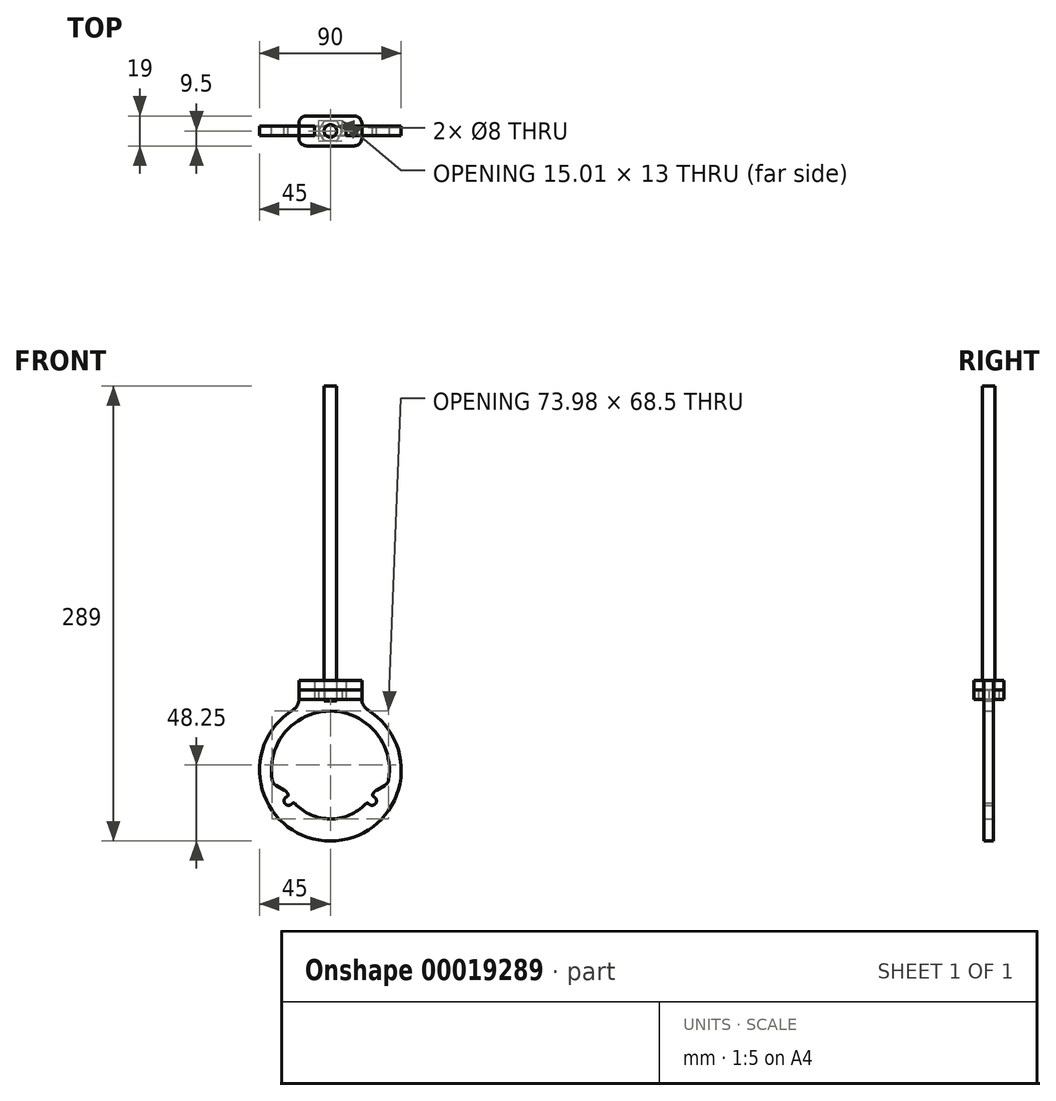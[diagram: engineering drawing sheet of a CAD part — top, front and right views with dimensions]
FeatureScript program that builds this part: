
annotation { "Feature Type Name" : "Feature", "Feature Type Description" : "" }
export const myFeature = defineFeature(function(context is Context, id is Id, definition is map)
    precondition{}
    {
        {
            var Q0;
            Q0=qCreatedBy(makeId("Front.planeOp"),FACE);
            var sketch = newSketch(context, id + "F0", { "sketchPlane" : qUnion([Q0])});
            skCircle(sketch, "E0", {"center": v(0, 0) * mm, "radius": 30 * mm, "construction": true});
            skArc(sketch, "E1", {"start": v(-29.8, -8.57) * mm, "mid": v(-33.82, -12.34) * mm, "end": v(-28.3, -12.64) * mm});
            skArc(sketch, "E2", {"start": v(-28.3, -12.64) * mm, "mid": v(0, -31) * mm, "end": v(28.3, -12.64) * mm});
            skArc(sketch, "E3.trimOffspring", {"start": v(29.8, -8.57) * mm, "mid": v(30.21, -6.95) * mm, "end": v(30.54, -5.31) * mm});
            skArc(sketch, "E4.trimOffspring", {"start": v(28.3, -12.64) * mm, "mid": v(33.82, -12.34) * mm, "end": v(29.8, -8.57) * mm});
            skArc(sketch, "E5.trimOffspring", {"start": v(34.92, 2.37) * mm, "mid": v(0, 35) * mm, "end": v(-34.92, 2.37) * mm});
            skArc(sketch, "E6", {"start": v(-34.92, 2.37) * mm, "mid": v(-33.89, -2.13) * mm, "end": v(-30.54, -5.31) * mm});
            skLineSegment(sketch, "E7", {"start": v(0, -11.31) * mm, "end": v(0, 0) * mm, "construction": true});
            skArc(sketch, "E8.0.MirrorCS", {"start": v(34.92, 2.37) * mm, "mid": v(33.89, -2.13) * mm, "end": v(30.54, -5.31) * mm});
            skArc(sketch, "E9.trimOffspring", {"start": v(-30.54, -5.31) * mm, "mid": v(-30.21, -6.95) * mm, "end": v(-29.8, -8.57) * mm});
            skLineSegment(sketch, "E10", {"start": v(-30.54, -5.31) * mm, "end": v(30.54, -5.31) * mm, "construction": true});
            skLineSegment(sketch, "E11", {"start": v(-31, -11.31) * mm, "end": v(31, -11.31) * mm, "construction": true});
            skLineSegment(sketch, "E12", {"start": v(-20, 57) * mm, "end": v(-10, 57) * mm});
            skLineSegment(sketch, "E13", {"start": v(20, 57) * mm, "end": v(20, 40.31) * mm});
            skLineSegment(sketch, "E14", {"start": v(-20, 57) * mm, "end": v(-20, 40.31) * mm});
            skPoint(sketch, "E15", {"position": v(0, 57) * mm});
            skArc(sketch, "E16", {"start": v(-20, 40.31) * mm, "mid": v(0, -45) * mm, "end": v(20, 40.31) * mm});
            skArc(sketch, "E17", {"start": v(20, 40.31) * mm, "mid": v(0, 45) * mm, "end": v(-20, 40.31) * mm, "construction": true});
            skLineSegment(sketch, "E18", {"start": v(-10, 57) * mm, "end": v(-10, 45) * mm});
            skLineSegment(sketch, "E19", {"start": v(10, 45) * mm, "end": v(10, 57) * mm});
            skLineSegment(sketch, "E20", {"start": v(-10, 45) * mm, "end": v(-4, 45) * mm});
            skLineSegment(sketch, "E21", {"start": v(10, 57) * mm, "end": v(20, 57) * mm});
            skLineSegment(sketch, "E22", {"start": v(-10, 57) * mm, "end": v(10, 57) * mm, "construction": true});
            skLineSegment(sketch, "E23", {"start": v(4, 45) * mm, "end": v(4, 44) * mm});
            skLineSegment(sketch, "E24", {"start": v(4, 44) * mm, "end": v(-4, 44) * mm});
            skLineSegment(sketch, "E25", {"start": v(-4, 44) * mm, "end": v(-4, 45) * mm});
            skLineSegment(sketch, "E26", {"start": v(4, 45) * mm, "end": v(10, 45) * mm});
            skLineSegment(sketch, "E27", {"start": v(-4, 45) * mm, "end": v(4, 45) * mm, "construction": true});
            skSolve(sketch);
        }
        {
            var Q0;
            Q0=qCreatedBy(makeId("Front.planeOp"),FACE);
            var sketch = newSketch(context, id + "F1", { "sketchPlane" : qUnion([Q0])});
            skArc(sketch, "E28.0", {"start": v(-20, 40.31) * mm, "mid": v(0, -45) * mm, "end": v(20, 40.31) * mm});
            skLineSegment(sketch, "E28.1", {"start": v(20, 57) * mm, "end": v(20, 40.31) * mm});
            skLineSegment(sketch, "E28.2", {"start": v(10, 57) * mm, "end": v(20, 57) * mm});
            skLineSegment(sketch, "E28.3", {"start": v(10, 45) * mm, "end": v(10, 57) * mm});
            skLineSegment(sketch, "E28.4", {"start": v(4, 45) * mm, "end": v(10, 45) * mm});
            skLineSegment(sketch, "E28.5", {"start": v(4, 45) * mm, "end": v(4, 44) * mm});
            skLineSegment(sketch, "E28.6", {"start": v(4, 44) * mm, "end": v(-4, 44) * mm});
            skLineSegment(sketch, "E28.7", {"start": v(-4, 44) * mm, "end": v(-4, 45) * mm});
            skLineSegment(sketch, "E28.8", {"start": v(-10, 45) * mm, "end": v(-4, 45) * mm});
            skLineSegment(sketch, "E28.9", {"start": v(-10, 57) * mm, "end": v(-10, 45) * mm});
            skLineSegment(sketch, "E28.10", {"start": v(-20, 57) * mm, "end": v(-10, 57) * mm});
            skLineSegment(sketch, "E28.11", {"start": v(-20, 57) * mm, "end": v(-20, 40.31) * mm});
            skCircle(sketch, "E29.0", {"center": v(0, 0) * mm, "radius": 30 * mm, "construction": true});
            skLineSegment(sketch, "E30", {"start": v(-37.5, 0) * mm, "end": v(37.5, 0) * mm, "construction": true});
            skLineSegment(sketch, "E31", {"start": v(-34.98, -13.52) * mm, "end": v(34.98, -13.52) * mm, "construction": true});
            skLineSegment(sketch, "E32", {"start": v(-32.02, -19.52) * mm, "end": v(32.02, -19.52) * mm, "construction": true});
            skLineSegment(sketch, "E33", {"start": v(0, 37.5) * mm, "end": v(0, -37.5) * mm, "construction": true});
            skLineSegment(sketch, "E34", {"start": v(-27.9, -13.52) * mm, "end": v(-36.51, -8.54) * mm});
            skLineSegment(sketch, "E35.0.MirrorCS", {"start": v(27.9, -13.52) * mm, "end": v(36.51, -8.54) * mm});
            skArc(sketch, "E36", {"start": v(27.9, -13.52) * mm, "mid": v(0, 31) * mm, "end": v(-27.9, -13.52) * mm, "construction": true});
            skArc(sketch, "E37", {"start": v(-27.9, -13.52) * mm, "mid": v(-27.05, -15.14) * mm, "end": v(-26.11, -16.7) * mm});
            skArc(sketch, "E38", {"start": v(-36.51, -8.54) * mm, "mid": v(0, -37.5) * mm, "end": v(36.51, -8.54) * mm, "construction": true});
            skArc(sketch, "E39", {"start": v(36.51, -8.54) * mm, "mid": v(0, 37.5) * mm, "end": v(-36.51, -8.54) * mm});
            skArc(sketch, "E40", {"start": v(26.13, -16.68) * mm, "mid": v(27.06, -15.13) * mm, "end": v(27.9, -13.52) * mm});
            skArc(sketch, "E41", {"start": v(23.63, -20.07) * mm, "mid": v(24.94, -18.42) * mm, "end": v(26.13, -16.68) * mm, "construction": true});
            skArc(sketch, "E42", {"start": v(-23.75, -19.92) * mm, "mid": v(-0.1, -31) * mm, "end": v(23.63, -20.07) * mm});
            skArc(sketch, "E43", {"start": v(-26.11, -16.7) * mm, "mid": v(-24.99, -18.35) * mm, "end": v(-23.75, -19.92) * mm, "construction": true});
            skArc(sketch, "E44", {"start": v(-23.75, -19.92) * mm, "mid": v(-24.28, -17.83) * mm, "end": v(-26.11, -16.7) * mm, "construction": true});
            skArc(sketch, "E45", {"start": v(-26.11, -16.7) * mm, "mid": v(-28.87, -21.2) * mm, "end": v(-23.75, -19.92) * mm});
            skArc(sketch, "E46", {"start": v(23.63, -20.07) * mm, "mid": v(24.13, -17.82) * mm, "end": v(26.13, -16.68) * mm, "construction": true});
            skArc(sketch, "E47", {"start": v(26.13, -16.68) * mm, "mid": v(28.72, -21.21) * mm, "end": v(23.63, -20.07) * mm});
            skSolve(sketch);
        }
        {
            var Q0;
            Q0=qSketchRegion(id+"F1",true);
            extrude(context, id + "F2", {"entities" : qUnion([Q0]), "depth" : 6 * mm});
        }
        {
            var Q0;
            Q0=makeQuery(id+"F2.opExtrude","SWEPT_FACE",FACE,{"disambiguationData":[OSD([sQuery(id+"F1.wireOp",EDGE,"E28.4")])]});
            var sketch = newSketch(context, id + "F3", { "sketchPlane" : qUnion([Q0])});
            skLineSegment(sketch, "E48.bottom", {"start": v(20, -12.5) * mm, "end": v(-20, -12.5) * mm});
            skLineSegment(sketch, "E48.top", {"start": v(20, 6.5) * mm, "end": v(-20, 6.5) * mm});
            skLineSegment(sketch, "E48.left", {"start": v(20, -12.5) * mm, "end": v(20, -6) * mm});
            skLineSegment(sketch, "E48.right", {"start": v(-20, -12.5) * mm, "end": v(-20, -6) * mm});
            skCircle(sketch, "E49.cCircle", {"center": v(0, -3) * mm, "radius": 6.5 * mm, "construction": true});
            skLineSegment(sketch, "E49.0", {"start": v(-3.75, -9.5) * mm, "end": v(-7.5, -3) * mm});
            skLineSegment(sketch, "E49.1", {"start": v(-7.5, -3) * mm, "end": v(-3.75, 3.5) * mm});
            skLineSegment(sketch, "E49.2", {"start": v(-3.75, 3.5) * mm, "end": v(3.75, 3.5) * mm});
            skLineSegment(sketch, "E49.3", {"start": v(3.75, 3.5) * mm, "end": v(7.5, -3) * mm});
            skLineSegment(sketch, "E49.4", {"start": v(7.5, -3) * mm, "end": v(3.75, -9.5) * mm});
            skLineSegment(sketch, "E49.5", {"start": v(3.75, -9.5) * mm, "end": v(-3.75, -9.5) * mm});
            skPoint(sketch, "E49.0.midPoint", {"position": v(-5.63, -6.25) * mm});
            skLineSegment(sketch, "E50", {"start": v(10, -3) * mm, "end": v(-10, -3) * mm, "construction": true});
            skLineSegment(sketch, "E51", {"start": v(-10, 0) * mm, "end": v(-10, -6) * mm});
            skLineSegment(sketch, "E52.trimOffspring", {"start": v(20, 0) * mm, "end": v(20, 6.5) * mm});
            skLineSegment(sketch, "E53", {"start": v(-20, 0) * mm, "end": v(-10, 0) * mm});
            skLineSegment(sketch, "E54", {"start": v(-10, -6) * mm, "end": v(-20, -6) * mm});
            skLineSegment(sketch, "E55.trimOffspring", {"start": v(-20, 0) * mm, "end": v(-20, 6.5) * mm});
            skLineSegment(sketch, "E56", {"start": v(20, -6) * mm, "end": v(10, -6) * mm});
            skLineSegment(sketch, "E57", {"start": v(10, -6) * mm, "end": v(10, 0) * mm});
            skLineSegment(sketch, "E58", {"start": v(10, 0) * mm, "end": v(20, 0) * mm});
            skSolve(sketch);
        }
        {
            var Q0;
            Q0=qSketchRegion(id+"F3",true);
            extrude(context, id + "F4", {"entities" : qUnion([Q0]), "depth" : 6 * mm});
        }
        {
            var Q0;
            Q0=makeQuery(id+"F4.opExtrude","CAP_FACE",FACE,{"disambiguationData":[OSD([sQuery(id+"F3.wireOp",EDGE,"E48.bottom"),sQuery(id+"F3.wireOp",EDGE,"E48.top"),sQuery(id+"F3.wireOp",EDGE,"E48.left"),sQuery(id+"F3.wireOp",EDGE,"E48.right"),sQuery(id+"F3.wireOp",EDGE,"E49.0"),sQuery(id+"F3.wireOp",EDGE,"E49.1"),sQuery(id+"F3.wireOp",EDGE,"E49.2"),sQuery(id+"F3.wireOp",EDGE,"E49.3"),sQuery(id+"F3.wireOp",EDGE,"E49.4"),sQuery(id+"F3.wireOp",EDGE,"E49.5"),sQuery(id+"F3.wireOp",EDGE,"E52.trimOffspring"),sQuery(id+"F3.wireOp",EDGE,"E53"),sQuery(id+"F3.wireOp",EDGE,"E51"),sQuery(id+"F3.wireOp",EDGE,"E54"),sQuery(id+"F3.wireOp",EDGE,"E55.trimOffspring"),sQuery(id+"F3.wireOp",EDGE,"E56"),sQuery(id+"F3.wireOp",EDGE,"E57"),sQuery(id+"F3.wireOp",EDGE,"E58")])],"isStart":false});
            var sketch = newSketch(context, id + "F5", { "sketchPlane" : qUnion([Q0])});
            skLineSegment(sketch, "E59", {"start": v(20, -12.5) * mm, "end": v(20, -6) * mm});
            skLineSegment(sketch, "E60", {"start": v(20, -6) * mm, "end": v(10, -6) * mm});
            skLineSegment(sketch, "E61", {"start": v(10, -6) * mm, "end": v(10, 0) * mm});
            skLineSegment(sketch, "E62", {"start": v(10, 0) * mm, "end": v(20, 0) * mm});
            skLineSegment(sketch, "E63", {"start": v(20, 0) * mm, "end": v(20, 6.5) * mm});
            skLineSegment(sketch, "E64", {"start": v(20, 6.5) * mm, "end": v(-20, 6.5) * mm});
            skLineSegment(sketch, "E65", {"start": v(-20, 6.5) * mm, "end": v(-20, 0) * mm});
            skLineSegment(sketch, "E66", {"start": v(-20, 0) * mm, "end": v(-10, 0) * mm});
            skLineSegment(sketch, "E67", {"start": v(-10, 0) * mm, "end": v(-10, -6) * mm});
            skLineSegment(sketch, "E68", {"start": v(-10, -6) * mm, "end": v(-20, -6) * mm});
            skLineSegment(sketch, "E69", {"start": v(-20, -6) * mm, "end": v(-20, -12.5) * mm});
            skLineSegment(sketch, "E70", {"start": v(-20, -12.5) * mm, "end": v(20, -12.5) * mm});
            skCircle(sketch, "E71", {"center": v(0, -3) * mm, "radius": 4 * mm});
            skSolve(sketch);
        }
        {
            var Q0;
            Q0=qSketchRegion(id+"F5",true);
            extrude(context, id + "F6", {"entities" : qUnion([Q0]), "depth" : 6 * mm});
        }
        {
            var Q0;
            Q0=makeQuery(id+"F2.opExtrude","SWEPT_FACE",FACE,{"disambiguationData":[OSD([sQuery(id+"F1.wireOp",EDGE,"E28.6")])]});
            var sketch = newSketch(context, id + "F7", { "sketchPlane" : qUnion([Q0])});
            skCircle(sketch, "E72.0", {"center": v(0, -3) * mm, "radius": 4 * mm});
            skSolve(sketch);
        }
        {
            var Q0;
            Q0=qSketchRegion(id+"F7",true);
            extrude(context, id + "F8", {"entities" : qUnion([Q0]), "depth" : 200 * mm});
        }
        {
            var Q0;
            Q0=makeQuery(id+"F8.opExtrude","CAP_EDGE",EDGE,{"disambiguationData":[OSD([sQuery(id+"F7.wireOp",EDGE,"E72.0")])],"isStart":true});
            fillet(context, id + "F9", {"entities" : qUnion([Q0]), "radius" : 1 * mm, "tangentPropagation" : true, "allowEdgeOverflow" : false});
        }
        {
            var Q0;
            Q0=makeQuery(id+"F4.opExtrude","CAP_FACE",FACE,{"disambiguationData":[OSD([sQuery(id+"F3.wireOp",EDGE,"E48.bottom"),sQuery(id+"F3.wireOp",EDGE,"E48.top"),sQuery(id+"F3.wireOp",EDGE,"E48.left"),sQuery(id+"F3.wireOp",EDGE,"E48.right"),sQuery(id+"F3.wireOp",EDGE,"E49.0"),sQuery(id+"F3.wireOp",EDGE,"E49.1"),sQuery(id+"F3.wireOp",EDGE,"E49.2"),sQuery(id+"F3.wireOp",EDGE,"E49.3"),sQuery(id+"F3.wireOp",EDGE,"E49.4"),sQuery(id+"F3.wireOp",EDGE,"E49.5"),sQuery(id+"F3.wireOp",EDGE,"E52.trimOffspring"),sQuery(id+"F3.wireOp",EDGE,"E53"),sQuery(id+"F3.wireOp",EDGE,"E51"),sQuery(id+"F3.wireOp",EDGE,"E54"),sQuery(id+"F3.wireOp",EDGE,"E55.trimOffspring"),sQuery(id+"F3.wireOp",EDGE,"E56"),sQuery(id+"F3.wireOp",EDGE,"E57"),sQuery(id+"F3.wireOp",EDGE,"E58")])],"isStart":true});
            var sketch = newSketch(context, id + "F10", { "sketchPlane" : qUnion([Q0])});
            skLineSegment(sketch, "E73.0", {"start": v(-3.75, -3.5) * mm, "end": v(3.75, -3.5) * mm});
            skLineSegment(sketch, "E73.1", {"start": v(3.75, -3.5) * mm, "end": v(7.5, 3) * mm});
            skLineSegment(sketch, "E73.2", {"start": v(7.5, 3) * mm, "end": v(3.75, 9.5) * mm});
            skLineSegment(sketch, "E73.3", {"start": v(3.75, 9.5) * mm, "end": v(-3.75, 9.5) * mm});
            skLineSegment(sketch, "E73.4", {"start": v(-3.75, 9.5) * mm, "end": v(-7.5, 3) * mm});
            skLineSegment(sketch, "E73.5", {"start": v(-7.5, 3) * mm, "end": v(-3.75, -3.5) * mm});
            skCircle(sketch, "E74", {"center": v(0, 3) * mm, "radius": 4 * mm});
            skSolve(sketch);
        }
        {
            var Q0;
            Q0=qSketchRegion(id+"F10",true);
            extrude(context, id + "F11", {"entities" : qUnion([Q0]), "oppositeDirection" : true, "depth" : 6 * mm});
        }
        {
            var Q0;
            Q0=makeQuery(id+"F11.opExtrude","CAP_FACE",FACE,{"disambiguationData":[OSD([sQuery(id+"F10.wireOp",EDGE,"E73.0"),sQuery(id+"F10.wireOp",EDGE,"E73.1"),sQuery(id+"F10.wireOp",EDGE,"E73.2"),sQuery(id+"F10.wireOp",EDGE,"E73.3"),sQuery(id+"F10.wireOp",EDGE,"E73.4"),sQuery(id+"F10.wireOp",EDGE,"E73.5"),sQuery(id+"F10.wireOp",EDGE,"E74")])],"isStart":true});
            fillet(context, id + "F12", {"entities" : qUnion([Q0]), "radius" : .5 * mm, "tangentPropagation" : true, "allowEdgeOverflow" : false});
        }
        {
            var Q0;
            Q0=makeQuery(id+"F2.opExtrude","SWEPT_EDGE",EDGE,{"disambiguationData":[OSD([sQuery(id+"F1.wireOp",EDGE,"E34"),sQuery(id+"F1.wireOp",EDGE,"E39")])]});
            var Q1;
            Q1=makeQuery(id+"F2.opExtrude","SWEPT_EDGE",EDGE,{"disambiguationData":[OSD([sQuery(id+"F1.wireOp",EDGE,"E34"),sQuery(id+"F1.wireOp",EDGE,"E37")])]});
            var Q2;
            Q2=makeQuery(id+"F2.opExtrude","SWEPT_EDGE",EDGE,{"disambiguationData":[OSD([sQuery(id+"F1.wireOp",EDGE,"E35.0.MirrorCS"),sQuery(id+"F1.wireOp",EDGE,"E40")])]});
            var Q3;
            Q3=makeQuery(id+"F2.opExtrude","SWEPT_EDGE",EDGE,{"disambiguationData":[OSD([sQuery(id+"F1.wireOp",EDGE,"E35.0.MirrorCS"),sQuery(id+"F1.wireOp",EDGE,"E39")])]});
            var Q4;
            Q4=makeQuery(id+"F6.opExtrude","SWEPT_EDGE",EDGE,{"disambiguationData":[OSD([sQuery(id+"F5.wireOp",EDGE,"E59"),sQuery(id+"F5.wireOp",EDGE,"E70")])]});
            var Q5;
            Q5=makeQuery(id+"F4.opExtrude","SWEPT_EDGE",EDGE,{"disambiguationData":[OSD([sQuery(id+"F3.wireOp",EDGE,"E48.bottom"),sQuery(id+"F3.wireOp",EDGE,"E48.left")])]});
            var Q6;
            Q6=makeQuery(id+"F4.opExtrude","SWEPT_EDGE",EDGE,{"disambiguationData":[OSD([sQuery(id+"F3.wireOp",EDGE,"E48.top"),sQuery(id+"F3.wireOp",EDGE,"E52.trimOffspring")])]});
            var Q7;
            Q7=makeQuery(id+"F6.opExtrude","SWEPT_EDGE",EDGE,{"disambiguationData":[OSD([sQuery(id+"F5.wireOp",EDGE,"E63"),sQuery(id+"F5.wireOp",EDGE,"E64")])]});
            var Q8;
            Q8=makeQuery(id+"F4.opExtrude","SWEPT_EDGE",EDGE,{"disambiguationData":[OSD([sQuery(id+"F3.wireOp",EDGE,"E48.bottom"),sQuery(id+"F3.wireOp",EDGE,"E48.right")])]});
            var Q9;
            Q9=makeQuery(id+"F6.opExtrude","SWEPT_EDGE",EDGE,{"disambiguationData":[OSD([sQuery(id+"F5.wireOp",EDGE,"E69"),sQuery(id+"F5.wireOp",EDGE,"E70")])]});
            var Q10;
            Q10=makeQuery(id+"F6.opExtrude","SWEPT_EDGE",EDGE,{"disambiguationData":[OSD([sQuery(id+"F5.wireOp",EDGE,"E64"),sQuery(id+"F5.wireOp",EDGE,"E65")])]});
            var Q11;
            Q11=makeQuery(id+"F4.opExtrude","SWEPT_EDGE",EDGE,{"disambiguationData":[OSD([sQuery(id+"F3.wireOp",EDGE,"E48.top"),sQuery(id+"F3.wireOp",EDGE,"E55.trimOffspring")])]});
            fillet(context, id + "F13", {"entities" : qUnion([Q0, Q1, Q2, Q3, Q4, Q5, Q6, Q7, Q8, Q9, Q10, Q11]), "radius" : 5 * mm, "tangentPropagation" : true, "allowEdgeOverflow" : false});
        }
        {
            var Q0;
            Q0=makeQuery(id+"F2.opExtrude","SWEPT_EDGE",EDGE,{"disambiguationData":[OSD([sQuery(id+"F1.wireOp",EDGE,"E37"),sQuery(id+"F1.wireOp",EDGE,"E45")])]});
            var Q1;
            Q1=makeQuery(id+"F2.opExtrude","SWEPT_EDGE",EDGE,{"disambiguationData":[OSD([sQuery(id+"F1.wireOp",EDGE,"E42"),sQuery(id+"F1.wireOp",EDGE,"E45")])]});
            var Q2;
            Q2=makeQuery(id+"F2.opExtrude","SWEPT_EDGE",EDGE,{"disambiguationData":[OSD([sQuery(id+"F1.wireOp",EDGE,"E42"),sQuery(id+"F1.wireOp",EDGE,"E47")])]});
            var Q3;
            Q3=makeQuery(id+"F2.opExtrude","SWEPT_EDGE",EDGE,{"disambiguationData":[OSD([sQuery(id+"F1.wireOp",EDGE,"E40"),sQuery(id+"F1.wireOp",EDGE,"E47")])]});
            fillet(context, id + "F14", {"entities" : qUnion([Q0, Q1, Q2, Q3]), "radius" : 1.25 * mm, "tangentPropagation" : true, "allowEdgeOverflow" : false});
        }
        {
            var Q0;
            Q0=makeQuery(id+"F2.opExtrude","SWEPT_EDGE",EDGE,{"disambiguationData":[OSD([sQuery(id+"F1.wireOp",EDGE,"E28.0"),sQuery(id+"F1.wireOp",EDGE,"E28.11")])]});
            var Q1;
            Q1=makeQuery(id+"F2.opExtrude","SWEPT_EDGE",EDGE,{"disambiguationData":[OSD([sQuery(id+"F1.wireOp",EDGE,"E28.0"),sQuery(id+"F1.wireOp",EDGE,"E28.1")])]});
            fillet(context, id + "F15", {"entities" : qUnion([Q0, Q1]), "radius" : 8 * mm, "tangentPropagation" : true, "allowEdgeOverflow" : false});
        }
    });
